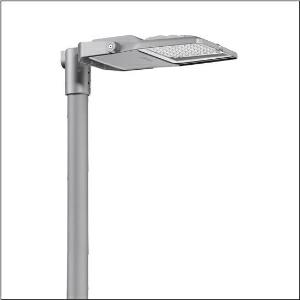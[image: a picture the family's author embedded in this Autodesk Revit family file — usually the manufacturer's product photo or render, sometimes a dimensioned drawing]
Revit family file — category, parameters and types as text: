
# Revit family: floodlight_fl_21_iq_mini___pl64_5xa7772d4e3a_9d14
name_source: partatom
category: Lighting Fixtures
units: mm (PartAtom-declared; Revit-internal decimal feet)

## family parameters
Cut with Voids When Loaded = No
Host = Face
Light Source = No
Part Type = Normal
Room Calculation Point = No
Round Connector Dimension = Use Diameter
Shared = No

## types (1)
- --- (1 x LED, 17970 lm, 143 W, 4000K)
    Apparent Load = 143 VA
    CIE Flux Codes = 28 80 98 100 100
    Color Rendering = 70
    Color Temperature = 4000K
    Default Elevation = 1800 mm
    Description = Floodlight FL 21 iQ mini, floodlight, primary light control with lens, of PMMA, primary optical cover: protective disc, of toughened safety glass, transparent, light distribution: PL64, light emission: direct distribution, installation type: surface-mounted, lamps: LED, High Power LED, rated values: 17.970lm | 143W | 125,7lm/W (begin service life); end service life: 17.970lm | 151,6W; at 50% lumin. flux: 8.985lm | 60,8W | 147,8lm/W, colour temperature: 4000K, colour rendering: CRI > 70, light colour: 740, light setting 1 begin service life: 100% | 17.970lm | 143W | 125,7lm/W | 4.000K, light setting 1 end service life: 151,6W, further light settings possible, control: Auto-Match, Temp-Guard, Night-Set, Smart-Wire, Desk-Remote (wireless, voltage-free reading and setting of iQ features in the workshop via application-optimized NFC function/RFID function), optimised constant luminous flux control (CLO 2.0), Light-Fading, Lumen-Switch, with terminal, 6-pole, mains connection: 220..240V, AC, 50/60Hz, luminaire housing, of diecast aluminium, powder-coated, Siteco® metallic grey (DB 702S), corrosivity category C5 mid according to DIN EN ISO 12944suitable for swimming poolschlorine-resistant, sealing non-destructively replaceable, please order mast flange separately, mast bracket, of steel, galvanised, powder-coated, protection rating (complete): IP66, insulation class (complete): insulation class II (safety insulation), certification: CE, ENEC, VDE, protection symbol: D, impact resistance: IK08, permissible operating ambient temperature: -40..+40°C, permissible operating ambient temperature for outdoor applications: -40..+50°C, standard: DIN EN 12944, LABS conformity tested according to VDMA 24364:2018-05, packaging unit: 1 piece

Light Distribution: PL64
    Height = 70 mm
    Lamp = 1 x LED
    Lamp Light Flux = 17970 lm
    Lamp Power = 143 W
    Lamp count = 1
    Length = 485 mm
    Luminous efficacy = 126 lm/W
    Manufacturer = Siteco
    ModVariant = No
    Model = 5XA7772D4E3A
    Number of Poles = 1
    OnlyDefault = Yes
    Power Factor = 1
    Product Name = Floodlight FL 21 iQ mini | PL64
    Product group = floodlight | pylon annexe
    ProductGroupID = 6201
    Protection Class = Protection class II
    Protection Degree = IP 66
    RLX_Detail_Level = 1
    RLX_Emergency_Light_Flux = 0 lm
    RLX_Emergency_Type = 0
    RLX_Emergency_Type_DB = No
    RlxData = <blob elided: 101761 chars, md5=69d1aac3>
    Socket = socket
    Standby Power = 0 W
    System Light Flux = 17970 lm
    System Power = 143 W
    Type Comments = factory setting: luminous flux: 100 % | dim-lin: 254 | 730 mA
    Type Image = l_1007125.jpg
    URL = http://relux.com
    VarID = @adj_168909
    Voltage = 0 V
    Weight = 0.00 kg
    Width = 337 mm

## geometry (parser evidence)
native form markers: Blend x4, Sweep x12
no freeform markers — native parametric forms only
